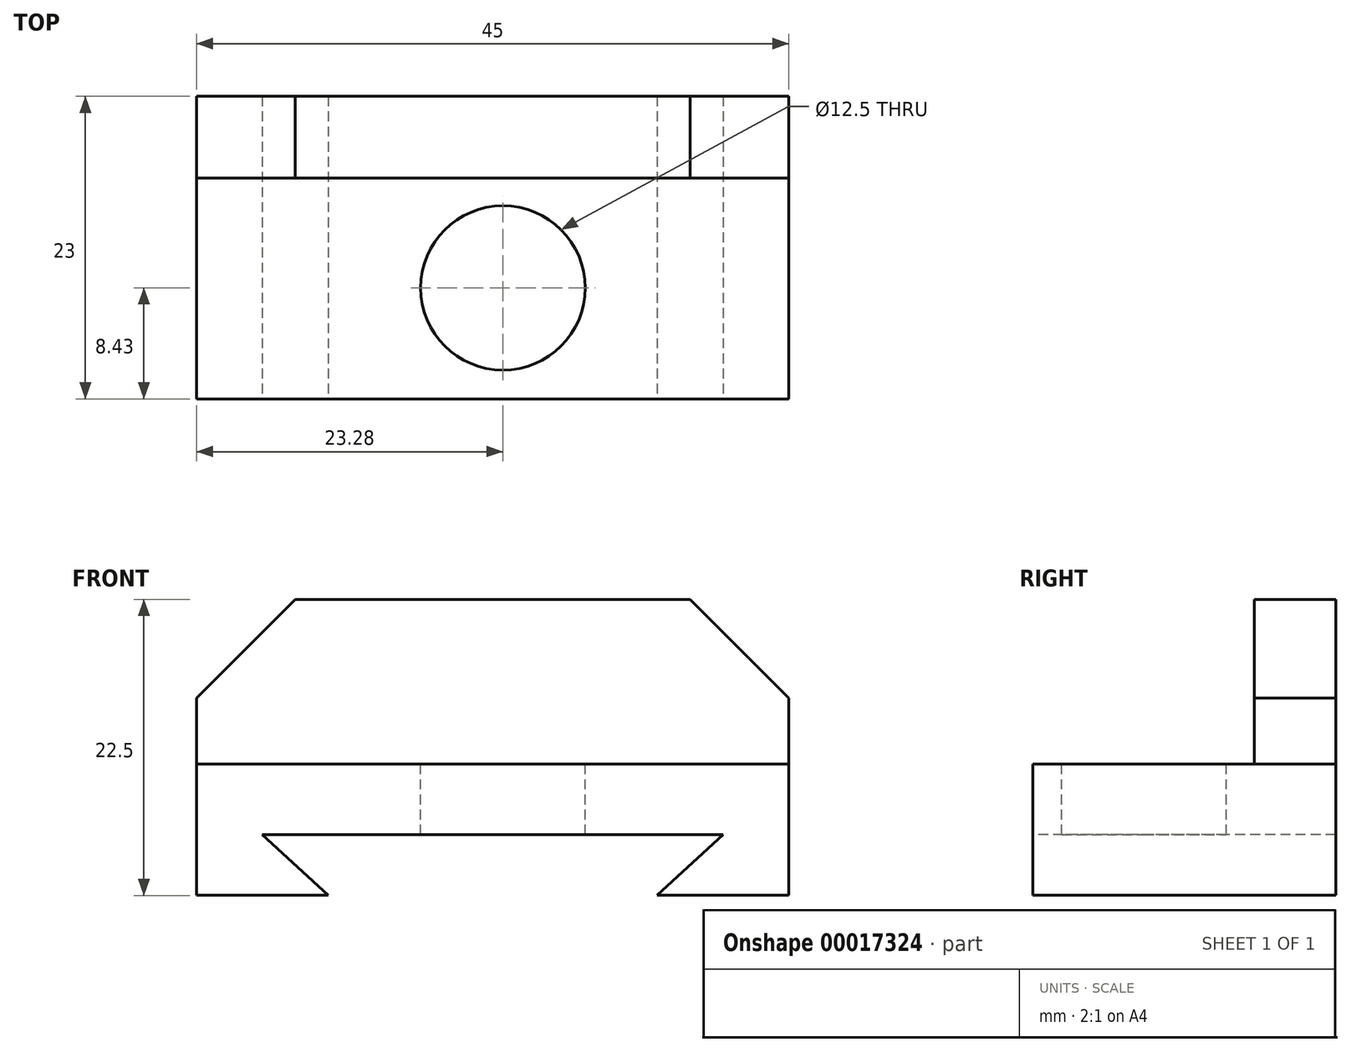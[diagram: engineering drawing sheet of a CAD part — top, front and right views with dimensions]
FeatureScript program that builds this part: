
annotation { "Feature Type Name" : "Feature", "Feature Type Description" : "" }
export const myFeature = defineFeature(function(context is Context, id is Id, definition is map)
    precondition{}
    {
        {
            var Q0;
            Q0=qCreatedBy(makeId("Front.planeOp"),FACE);
            var sketch = newSketch(context, id + "F0", { "sketchPlane" : qUnion([Q0])});
            skLineSegment(sketch, "E0", {"start": v(-23.28, -11.53) * mm, "end": v(21.72, -11.53) * mm});
            skLineSegment(sketch, "E1", {"start": v(21.72, -11.53) * mm, "end": v(21.72, -21.53) * mm});
            skLineSegment(sketch, "E2", {"start": v(-23.28, -11.53) * mm, "end": v(-23.28, -21.53) * mm});
            skLineSegment(sketch, "E3", {"start": v(-23.28, -21.53) * mm, "end": v(-13.28, -21.53) * mm});
            skLineSegment(sketch, "E4", {"start": v(21.72, -21.53) * mm, "end": v(11.72, -21.53) * mm});
            skLineSegment(sketch, "E5", {"start": v(11.72, -21.53) * mm, "end": v(16.72, -16.9) * mm});
            skLineSegment(sketch, "E6", {"start": v(16.72, -16.9) * mm, "end": v(-18.28, -16.9) * mm});
            skLineSegment(sketch, "E7", {"start": v(-18.28, -16.9) * mm, "end": v(-13.28, -21.53) * mm});
            skPoint(sketch, "E8", {"position": v(16.72, -21.53) * mm});
            skPoint(sketch, "E9", {"position": v(-18.28, -21.53) * mm});
            skSolve(sketch);
        }
        {
            var Q0;
            Q0=makeQuery(id+"F0.imprint","IMPRINT",FACE,{"disambiguationData":[TD([[makeQuery(id+"F0.imprint","IMPRINT",EDGE,{"derivedFrom":sQuery(id+"F0.wireOp",EDGE,"E0")}),-1.0]])]});
            extrude(context, id + "F1", {"entities" : qUnion([Q0]), "oppositeDirection" : true, "depth" : 23 * mm});
        }
        {
            var Q0;
            Q0=makeQuery(id+"F1.opExtrude","SWEPT_FACE",FACE,{"disambiguationData":[OSD([sQuery(id+"F0.wireOp",EDGE,"E0")])]});
            var sketch = newSketch(context, id + "F2", { "sketchPlane" : qUnion([Q0])});
            skPoint(sketch, "E10", {"position": v(0, 2.13) * mm});
            skPoint(sketch, "E11", {"position": v(0, 8.43) * mm});
            skSolve(sketch);
        }
        {
            var Q0;
            Q0=sQuery(id+"F2.wireOp",VERTEX,"E11");
            var Q1;
            Q1=makeQuery(id+"F1.opExtrude","SWEPT_BODY",BODY,{"disambiguationData":[OSD([sQuery(id+"F0.wireOp",EDGE,"E0"),sQuery(id+"F0.wireOp",EDGE,"E1"),sQuery(id+"F0.wireOp",EDGE,"E2"),sQuery(id+"F0.wireOp",EDGE,"E3"),sQuery(id+"F0.wireOp",EDGE,"E4"),sQuery(id+"F0.wireOp",EDGE,"E5"),sQuery(id+"F0.wireOp",EDGE,"E6"),sQuery(id+"F0.wireOp",EDGE,"E7")])]});
            hole(context, id + "F3", {"style" : HoleStyle.SIMPLE, "holeDiameter" : 12.5 * mm, "endStyle" : HoleEndStyle.THROUGH, "locations" : qUnion([Q0]), "scope" : qUnion([Q1])});
        }
        {
            var Q0;
            Q0=makeQuery(id+"F1.opExtrude","CAP_FACE",FACE,{"disambiguationData":[OSD([sQuery(id+"F0.wireOp",EDGE,"E0"),sQuery(id+"F0.wireOp",EDGE,"E1"),sQuery(id+"F0.wireOp",EDGE,"E2"),sQuery(id+"F0.wireOp",EDGE,"E3"),sQuery(id+"F0.wireOp",EDGE,"E4"),sQuery(id+"F0.wireOp",EDGE,"E5"),sQuery(id+"F0.wireOp",EDGE,"E6"),sQuery(id+"F0.wireOp",EDGE,"E7")])],"isStart":false});
            var sketch = newSketch(context, id + "F4", { "sketchPlane" : qUnion([Q0])});
            skLineSegment(sketch, "E12", {"start": v(-21.72, -11.53) * mm, "end": v(-21.72, -6.53) * mm});
            skLineSegment(sketch, "E13", {"start": v(-14.22, 0.97) * mm, "end": v(15.78, 0.97) * mm});
            skLineSegment(sketch, "E14", {"start": v(23.28, -6.53) * mm, "end": v(23.28, -11.53) * mm});
            skLineSegment(sketch, "E15", {"start": v(23.28, -6.53) * mm, "end": v(15.78, 0.97) * mm});
            skLineSegment(sketch, "E16", {"start": v(-14.22, 0.97) * mm, "end": v(-21.72, -6.53) * mm});
            skSolve(sketch);
        }
        {
            var Q0;
            Q0=makeQuery(id+"F4.imprint","IMPRINT",FACE,{"disambiguationData":[TD([[makeQuery(id+"F4.imprint","IMPRINT",EDGE,{"derivedFrom":sQuery(id+"F4.wireOp",EDGE,"E12")}),-1.0]])]});
            extrude(context, id + "F5", {"entities" : qUnion([Q0]), "oppositeDirection" : true, "depth" : 6.2 * mm});
        }
    });
